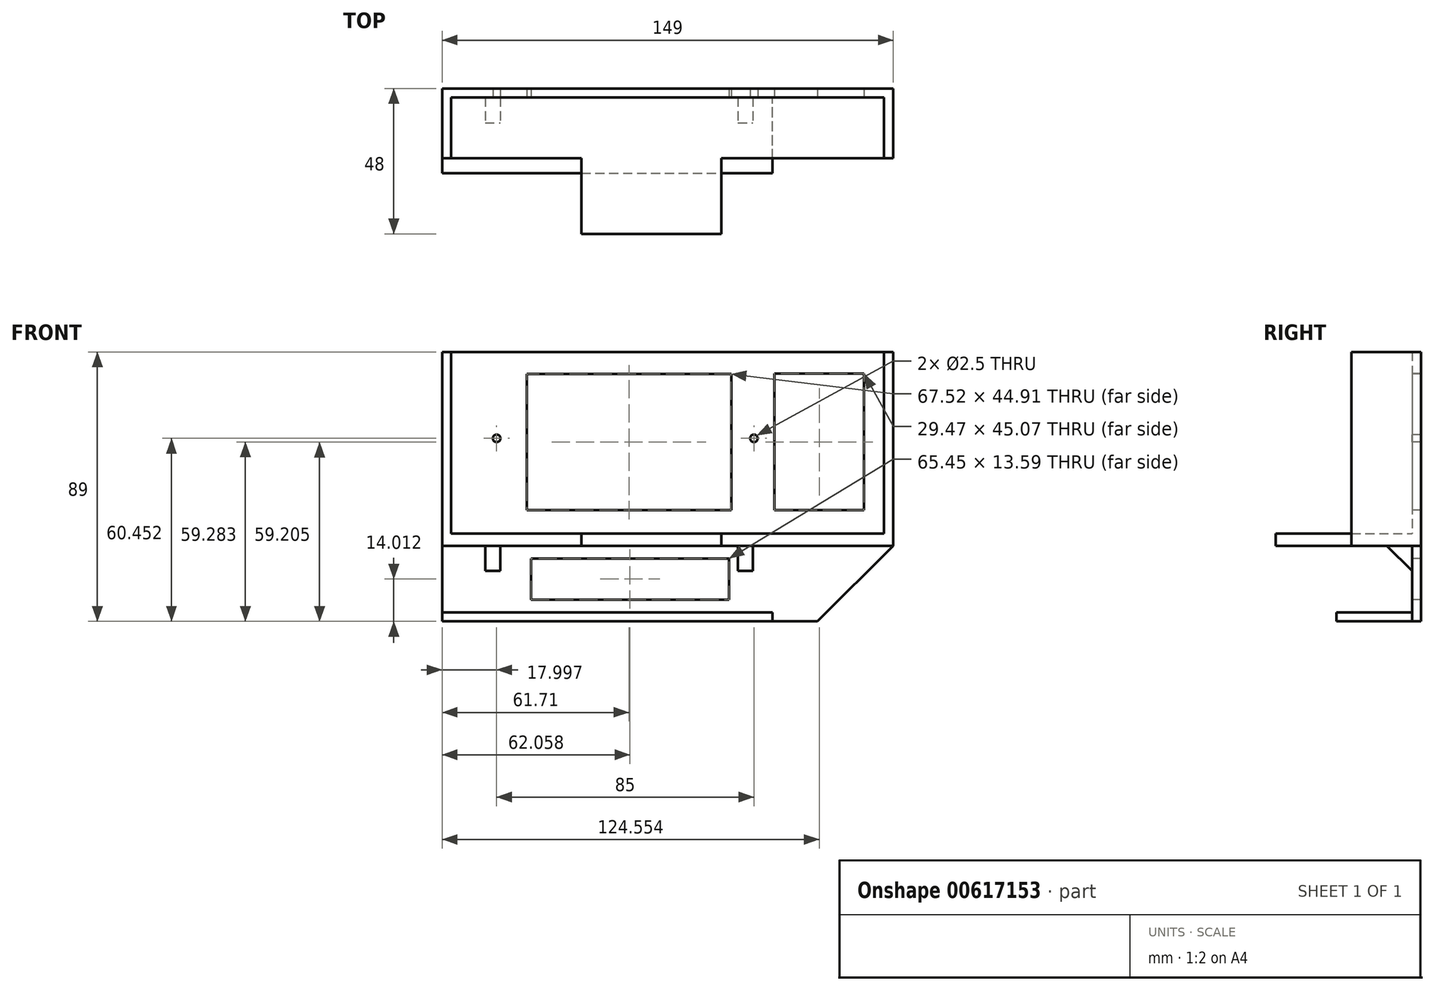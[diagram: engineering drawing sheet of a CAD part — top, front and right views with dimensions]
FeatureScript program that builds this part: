
annotation { "Feature Type Name" : "Feature", "Feature Type Description" : "" }
export const myFeature = defineFeature(function(context is Context, id is Id, definition is map)
    precondition{}
    {
        {
            var Q0;
            Q0=qCreatedBy(makeId("Front.planeOp"),FACE);
            var sketch = newSketch(context, id + "F0", { "sketchPlane" : qUnion([Q0])});
            skLineSegment(sketch, "E0.bottom", {"start": v(-34.14, 33.46) * mm, "end": v(112.86, 33.46) * mm});
            skLineSegment(sketch, "E0.top", {"start": v(-34.14, -26.54) * mm, "end": v(112.86, -26.54) * mm});
            skLineSegment(sketch, "E0.left", {"start": v(-34.14, 33.46) * mm, "end": v(-34.14, -26.54) * mm});
            skLineSegment(sketch, "E0.right", {"start": v(112.86, 33.46) * mm, "end": v(112.86, -26.54) * mm});
            skSolve(sketch);
        }
        {
            var Q0;
            Q0 = qSketchRegion(id + "F0", true);
            extrude(context, id + "F1", {"entities" : qUnion([Q0]), "depth" : 3 * mm, "offsetDistance" : 25 * mm});
        }
        {
            var Q0;
            Q0=makeQuery(id+"F1.opExtrude","CAP_FACE",FACE,{"disambiguationData":[OSD([sQuery(id+"F0.wireOp",EDGE,"E0.bottom"),sQuery(id+"F0.wireOp",EDGE,"E0.top"),sQuery(id+"F0.wireOp",EDGE,"E0.left"),sQuery(id+"F0.wireOp",EDGE,"E0.right")])],"isStart":false});
            var sketch = newSketch(context, id + "F2", { "sketchPlane" : qUnion([Q0])});
            skLineSegment(sketch, "E1.bottom", {"start": v(-34.14, 33.46) * mm, "end": v(-31.14, 33.46) * mm});
            skLineSegment(sketch, "E1.top", {"start": v(-34.14, -26.54) * mm, "end": v(-31.14, -26.54) * mm});
            skLineSegment(sketch, "E1.left", {"start": v(-34.14, 33.46) * mm, "end": v(-34.14, -26.54) * mm});
            skLineSegment(sketch, "E1.right", {"start": v(-31.14, 33.46) * mm, "end": v(-31.14, -26.54) * mm});
            skLineSegment(sketch, "E2.bottom", {"start": v(112.86, 33.46) * mm, "end": v(109.86, 33.46) * mm});
            skLineSegment(sketch, "E2.top", {"start": v(112.86, -26.54) * mm, "end": v(109.86, -26.54) * mm});
            skLineSegment(sketch, "E2.left", {"start": v(112.86, 33.46) * mm, "end": v(112.86, -26.54) * mm});
            skLineSegment(sketch, "E2.right", {"start": v(109.86, 33.46) * mm, "end": v(109.86, -26.54) * mm});
            skSolve(sketch);
        }
        {
            var Q0;
            Q0 = qSketchRegion(id + "F2", true);
            extrude(context, id + "F3", {"entities" : qUnion([Q0]), "operationType" : NewBodyOperationType.ADD, "depth" : 20 * mm, "offsetDistance" : 25 * mm});
        }
        {
            var Q0;
            Q0=makeQuery(id+"F3.boolean.opBoolean","MERGE",FACE,{"derivedFrom":[makeQuery(id+"F1.opExtrude","SWEPT_FACE",FACE,{"disambiguationData":[OSD([sQuery(id+"F0.wireOp",EDGE,"E0.top")])]}),makeQuery(id+"F3.opExtrude","SWEPT_FACE",FACE,{"disambiguationData":[OSD([sQuery(id+"F2.wireOp",EDGE,"E1.top")])]}),makeQuery(id+"F3.opExtrude","SWEPT_FACE",FACE,{"disambiguationData":[OSD([sQuery(id+"F2.wireOp",EDGE,"E2.top")])]})]});
            extrude(context, id + "F4", {"entities" : qUnion([Q0]), "operationType" : NewBodyOperationType.ADD, "depth" : 4 * mm, "offsetDistance" : 25 * mm});
        }
        {
            var Q0;
            {var subQ0=sQuery(id+"F0.wireOp",EDGE,"E0.top");Q0=makeQuery(id+"F4.boolean.opBoolean","MERGE",FACE,{"derivedFrom":[makeQuery(id+"F1.opExtrude","CAP_FACE",FACE,{"disambiguationData":[OSD([sQuery(id+"F0.wireOp",EDGE,"E0.bottom"),subQ0,sQuery(id+"F0.wireOp",EDGE,"E0.left"),sQuery(id+"F0.wireOp",EDGE,"E0.right")])],"isStart":false}),makeQuery(id+"F4.opExtrude","SWEPT_FACE",FACE,{"disambiguationData":[OSD([subQ0]),TDD([makeQuery(id+"F1.opExtrude","CAP_EDGE",EDGE,{"disambiguationData":[OSD([subQ0])],"isStart":false})])]})]});}
            var sketch = newSketch(context, id + "F5", { "sketchPlane" : qUnion([Q0])});
            skLineSegment(sketch, "E3.bottom", {"start": v(-31.14, -30.54) * mm, "end": v(109.86, -30.54) * mm});
            skLineSegment(sketch, "E3.top", {"start": v(-31.14, -26.54) * mm, "end": v(109.86, -26.54) * mm});
            skLineSegment(sketch, "E3.left", {"start": v(-31.14, -30.54) * mm, "end": v(-31.14, -26.54) * mm});
            skLineSegment(sketch, "E3.right", {"start": v(109.86, -30.54) * mm, "end": v(109.86, -26.54) * mm});
            skSolve(sketch);
        }
        {
            var Q0;
            Q0 = qSketchRegion(id + "F5", true);
            extrude(context, id + "F6", {"entities" : qUnion([Q0]), "operationType" : NewBodyOperationType.ADD, "depth" : 20 * mm, "offsetDistance" : 25 * mm});
        }
        {
            var Q0;
            {var subQ0=sQuery(id+"F2.wireOp",EDGE,"E2.left");var subQ1=sQuery(id+"F0.wireOp",EDGE,"E0.right");Q0=makeQuery(id+"F4.boolean.opBoolean","MERGE",FACE,{"derivedFrom":[makeQuery(id+"F3.boolean.opBoolean","MERGE",FACE,{"derivedFrom":[makeQuery(id+"F1.opExtrude","SWEPT_FACE",FACE,{"disambiguationData":[OSD([subQ1])]}),makeQuery(id+"F3.opExtrude","SWEPT_FACE",FACE,{"disambiguationData":[OSD([subQ0])]})]}),makeQuery(id+"F4.opExtrude","SWEPT_FACE",FACE,{"disambiguationData":[OSD([sQuery(id+"F0.wireOp",EDGE,"E0.top"),subQ1,sQuery(id+"F2.wireOp",EDGE,"E2.top"),subQ0])]})]});}
            extrude(context, id + "F7", {"entities" : qUnion([Q0]), "operationType" : NewBodyOperationType.ADD, "depth" : 2 * mm, "offsetDistance" : 25 * mm});
        }
        {
            var Q0;
            {var subQ0=sQuery(id+"F2.wireOp",EDGE,"E2.right");Q0=makeQuery(id+"F4.boolean.opBoolean","MERGE",FACE,{"derivedFrom":[makeQuery(id+"F3.opExtrude","SWEPT_FACE",FACE,{"disambiguationData":[OSD([subQ0])]}),makeQuery(id+"F4.opExtrude","SWEPT_FACE",FACE,{"disambiguationData":[OSD([sQuery(id+"F0.wireOp",EDGE,"E0.top"),sQuery(id+"F2.wireOp",EDGE,"E2.top"),subQ0])]})]});}
            extrude(context, id + "F8", {"entities" : qUnion([Q0]), "operationType" : NewBodyOperationType.REMOVE, "oppositeDirection" : true, "depth" : 2 * mm, "offsetDistance" : 25 * mm});
        }
        {
            var Q0;
            {var subQ0=sQuery(id+"F2.wireOp",EDGE,"E2.right");var subQ1=sQuery(id+"F2.wireOp",EDGE,"E2.top");var subQ2=sQuery(id+"F0.wireOp",EDGE,"E0.top");Q0=makeQuery(id+"F8.boolean.opBoolean","MERGE",FACE,{"derivedFrom":[makeQuery(id+"F4.boolean.opBoolean","MERGE",FACE,{"derivedFrom":[makeQuery(id+"F1.opExtrude","CAP_FACE",FACE,{"disambiguationData":[OSD([sQuery(id+"F0.wireOp",EDGE,"E0.bottom"),subQ2,sQuery(id+"F0.wireOp",EDGE,"E0.left"),sQuery(id+"F0.wireOp",EDGE,"E0.right")])],"isStart":false}),makeQuery(id+"F4.opExtrude","SWEPT_FACE",FACE,{"disambiguationData":[OSD([subQ2]),TDD([makeQuery(id+"F1.opExtrude","CAP_EDGE",EDGE,{"disambiguationData":[OSD([subQ2])],"isStart":false})])]})]}),makeQuery(id+"F8.opExtrude","SWEPT_FACE",FACE,{"disambiguationData":[OSD([subQ2,subQ1,subQ0]),TDD([makeQuery(id+"F4.boolean.opBoolean","MERGE",EDGE,{"derivedFrom":[makeQuery(id+"F3.opExtrude","CAP_EDGE",EDGE,{"disambiguationData":[OSD([subQ0])],"isStart":true}),makeQuery(id+"F4.opExtrude","SWEPT_EDGE",EDGE,{"disambiguationData":[OSD([subQ2,subQ1,subQ0]),TDD([makeQuery(id+"F3.opExtrude","CAP_VERTEX",VERTEX,{"disambiguationData":[OSD([subQ2,subQ1,subQ0])],"isStart":true})])]})]})])]})]});}
            var sketch = newSketch(context, id + "F9", { "sketchPlane" : qUnion([Q0])});
            skCircle(sketch, "E4", {"center": v(-16.14, 4.91) * mm, "radius": 1.25 * mm});
            skCircle(sketch, "E5", {"center": v(68.86, 4.91) * mm, "radius": 1.25 * mm});
            skSolve(sketch);
        }
        {
            var Q0;
            {var subQ0=sQuery(id+"F2.wireOp",EDGE,"E2.top");var subQ1=sQuery(id+"F0.wireOp",EDGE,"E0.top");Q0=makeQuery(id+"F7.boolean.opBoolean","MERGE",FACE,{"derivedFrom":[makeQuery(id+"F6.boolean.opBoolean","MERGE",FACE,{"derivedFrom":[makeQuery(id+"F4.opExtrude","CAP_FACE",FACE,{"disambiguationData":[OSD([subQ1,sQuery(id+"F2.wireOp",EDGE,"E1.top"),subQ0])],"isStart":false}),makeQuery(id+"F6.opExtrude","SWEPT_FACE",FACE,{"disambiguationData":[OSD([sQuery(id+"F5.wireOp",EDGE,"E3.bottom")])]})]}),makeQuery(id+"F7.opExtrude","SWEPT_FACE",FACE,{"disambiguationData":[OSD([subQ1,sQuery(id+"F0.wireOp",EDGE,"E0.right"),subQ0,sQuery(id+"F2.wireOp",EDGE,"E2.left")])]})]});}
            var sketch = newSketch(context, id + "F10", { "sketchPlane" : qUnion([Q0])});
            skLineSegment(sketch, "E6.bottom", {"start": v(-19.9, 0) * mm, "end": v(-14.9, 0) * mm});
            skLineSegment(sketch, "E6.top", {"start": v(-19.9, 11.3) * mm, "end": v(-14.9, 11.3) * mm});
            skLineSegment(sketch, "E6.left", {"start": v(-19.9, 0) * mm, "end": v(-19.9, 11.3) * mm});
            skLineSegment(sketch, "E6.right", {"start": v(-14.9, 0) * mm, "end": v(-14.9, 11.3) * mm});
            skLineSegment(sketch, "E7.bottom", {"start": v(63.56, 0) * mm, "end": v(68.56, 0) * mm});
            skLineSegment(sketch, "E7.top", {"start": v(63.56, 11.3) * mm, "end": v(68.56, 11.3) * mm});
            skLineSegment(sketch, "E7.left", {"start": v(63.56, 0) * mm, "end": v(63.56, 11.3) * mm});
            skLineSegment(sketch, "E7.right", {"start": v(68.56, 0) * mm, "end": v(68.56, 11.3) * mm});
            skSolve(sketch);
        }
        {
            var Q0;
            Q0=makeQuery(id+"F10.imprint","IMPRINT",FACE,{"disambiguationData":[TD([[makeQuery(id+"F10.imprint","IMPRINT",EDGE,{"derivedFrom":sQuery(id+"F10.wireOp",EDGE,"E6.bottom")}),1.0]])]});
            var Q1;
            Q1=makeQuery(id+"F10.imprint","IMPRINT",FACE,{"disambiguationData":[TD([[makeQuery(id+"F10.imprint","IMPRINT",EDGE,{"derivedFrom":sQuery(id+"F10.wireOp",EDGE,"E7.bottom")}),1.0]])]});
            extrude(context, id + "F11", {"entities" : qUnion([Q0, Q1]), "operationType" : NewBodyOperationType.ADD, "depth" : 15 * mm, "offsetDistance" : 25 * mm});
        }
        {
            var Q0;
            Q0=makeQuery(id+"F9.imprint","IMPRINT",FACE,{"disambiguationData":[TD([[makeQuery(id+"F9.imprint","IMPRINT",EDGE,{"derivedFrom":sQuery(id+"F9.wireOp",EDGE,"E4")}),1.0]])]});
            var Q1;
            Q1=makeQuery(id+"F9.imprint","IMPRINT",FACE,{"disambiguationData":[TD([[makeQuery(id+"F9.imprint","IMPRINT",EDGE,{"derivedFrom":sQuery(id+"F9.wireOp",EDGE,"E5")}),1.0]])]});
            extrude(context, id + "F12", {"entities" : qUnion([Q0, Q1]), "operationType" : NewBodyOperationType.REMOVE, "oppositeDirection" : true, "depth" : 25 * mm, "offsetDistance" : 25 * mm});
        }
        {
            var Q0;
            Q0=makeQuery(id+"F11.opExtrude","CAP_EDGE",EDGE,{"disambiguationData":[OSD([sQuery(id+"F10.wireOp",EDGE,"E6.top")])],"isStart":false});
            var Q1;
            Q1=makeQuery(id+"F11.opExtrude","CAP_EDGE",EDGE,{"disambiguationData":[OSD([sQuery(id+"F10.wireOp",EDGE,"E7.top")])],"isStart":false});
            chamfer(context, id + "F13", {"entities" : qUnion([Q0, Q1]), "width" : 15 * mm, "tangentPropagation" : true});
        }
        {
            var Q0;
            {var subQ0=sQuery(id+"F2.wireOp",EDGE,"E2.top");var subQ1=sQuery(id+"F0.wireOp",EDGE,"E0.top");Q0=makeQuery(id+"F7.boolean.opBoolean","MERGE",FACE,{"derivedFrom":[makeQuery(id+"F6.boolean.opBoolean","MERGE",FACE,{"derivedFrom":[makeQuery(id+"F4.opExtrude","CAP_FACE",FACE,{"disambiguationData":[OSD([subQ1,sQuery(id+"F2.wireOp",EDGE,"E1.top"),subQ0])],"isStart":false}),makeQuery(id+"F6.opExtrude","SWEPT_FACE",FACE,{"disambiguationData":[OSD([sQuery(id+"F5.wireOp",EDGE,"E3.bottom")])]})]}),makeQuery(id+"F7.opExtrude","SWEPT_FACE",FACE,{"disambiguationData":[OSD([subQ1,sQuery(id+"F0.wireOp",EDGE,"E0.right"),subQ0,sQuery(id+"F2.wireOp",EDGE,"E2.left")])]})]});}
            var sketch = newSketch(context, id + "F14", { "sketchPlane" : qUnion([Q0])});
            skLineSegment(sketch, "E8.bottom", {"start": v(-34.14, 0) * mm, "end": v(114.86, 0) * mm});
            skLineSegment(sketch, "E8.top", {"start": v(-34.14, 3) * mm, "end": v(114.86, 3) * mm});
            skLineSegment(sketch, "E8.left", {"start": v(-34.14, 0) * mm, "end": v(-34.14, 3) * mm});
            skLineSegment(sketch, "E8.right", {"start": v(114.86, 0) * mm, "end": v(114.86, 3) * mm});
            skSolve(sketch);
        }
        {
            var Q0;
            {var subQ0=sQuery(id+"F14.wireOp",EDGE,"E8.left");Q0=makeQuery(id+"F14.imprint","IMPRINT",FACE,{"disambiguationData":[TD([[makeQuery(id+"F14.imprint","IMPRINT",EDGE,{"derivedFrom":subQ0}),1.0]])]});}
            var Q1;
            {var subQ0=sQuery(id+"F14.wireOp",EDGE,"E8.right");Q1=makeQuery(id+"F14.imprint","IMPRINT",FACE,{"disambiguationData":[TD([[makeQuery(id+"F14.imprint","IMPRINT",EDGE,{"derivedFrom":subQ0}),-1.0]])]});}
            var Q2;
            {var subQ0=sQuery(id+"F14.wireOp",EDGE,"E8.bottom");var subQ1=makeQuery(id+"F11.opExtrude","CAP_EDGE",EDGE,{"disambiguationData":[OSD([sQuery(id+"F10.wireOp",EDGE,"E6.left")])],"isStart":true});var subQ2=makeQuery(id+"F14.imprint","INTERSECT",VERTEX,{"derivedFrom":[subQ1,subQ0]});Q2=makeQuery(id+"F14.imprint","IMPRINT",FACE,{"disambiguationData":[TD([[makeQuery(id+"F14.imprint","IMPRINT",EDGE,{"disambiguationData":[TD([[subQ2,-1.0]])],"derivedFrom":subQ0}),1.0]])]});}
            var Q3;
            {var subQ0=sQuery(id+"F14.wireOp",EDGE,"E8.bottom");var subQ1=makeQuery(id+"F11.opExtrude","CAP_EDGE",EDGE,{"disambiguationData":[OSD([sQuery(id+"F10.wireOp",EDGE,"E7.left")])],"isStart":true});var subQ2=makeQuery(id+"F14.imprint","INTERSECT",VERTEX,{"derivedFrom":[subQ1,subQ0]});Q3=makeQuery(id+"F14.imprint","IMPRINT",FACE,{"disambiguationData":[TD([[makeQuery(id+"F14.imprint","IMPRINT",EDGE,{"disambiguationData":[TD([[subQ2,-1.0]])],"derivedFrom":subQ0}),1.0]])]});}
            var Q4;
            {var subQ0=sQuery(id+"F14.wireOp",EDGE,"E8.bottom");var subQ1=makeQuery(id+"F11.opExtrude","CAP_EDGE",EDGE,{"disambiguationData":[OSD([sQuery(id+"F10.wireOp",EDGE,"E6.right")])],"isStart":true});var subQ2=makeQuery(id+"F14.imprint","INTERSECT",VERTEX,{"derivedFrom":[subQ1,subQ0]});Q4=makeQuery(id+"F14.imprint","IMPRINT",FACE,{"disambiguationData":[TD([[makeQuery(id+"F14.imprint","IMPRINT",EDGE,{"disambiguationData":[TD([[subQ2,-1.0]])],"derivedFrom":subQ0}),1.0]])]});}
            extrude(context, id + "F15", {"entities" : qUnion([Q0, Q1, Q2, Q3, Q4]), "operationType" : NewBodyOperationType.ADD, "depth" : 25 * mm, "offsetDistance" : 25 * mm});
        }
        {
            var Q0;
            Q0=makeQuery(id+"F15.opExtrude","CAP_EDGE",EDGE,{"disambiguationData":[OSD([sQuery(id+"F14.wireOp",EDGE,"E8.right")])],"isStart":false});
            chamfer(context, id + "F16", {"entities" : qUnion([Q0]), "width" : 25 * mm, "tangentPropagation" : true});
        }
        {
            var Q0;
            Q0=makeQuery(id+"F15.opExtrude","SWEPT_FACE",FACE,{"disambiguationData":[OSD([sQuery(id+"F14.wireOp",EDGE,"E8.top")])]});
            var sketch = newSketch(context, id + "F17", { "sketchPlane" : qUnion([Q0])});
            skLineSegment(sketch, "E9.bottom", {"start": v(-34.14, -55.54) * mm, "end": v(74.97, -55.54) * mm});
            skLineSegment(sketch, "E9.top", {"start": v(-34.14, -52.54) * mm, "end": v(74.97, -52.54) * mm});
            skLineSegment(sketch, "E9.left", {"start": v(-34.14, -55.54) * mm, "end": v(-34.14, -52.54) * mm});
            skLineSegment(sketch, "E9.right", {"start": v(74.97, -55.54) * mm, "end": v(74.97, -52.54) * mm});
            skSolve(sketch);
        }
        {
            var Q0;
            Q0 = qSketchRegion(id + "F17", true);
            extrude(context, id + "F18", {"entities" : qUnion([Q0]), "operationType" : NewBodyOperationType.ADD, "depth" : 25 * mm, "offsetDistance" : 25 * mm});
        }
        {
            var Q0;
            {var subQ0=sQuery(id+"F2.wireOp",EDGE,"E2.right");var subQ1=sQuery(id+"F2.wireOp",EDGE,"E2.top");var subQ2=sQuery(id+"F0.wireOp",EDGE,"E0.top");Q0=makeQuery(id+"F8.boolean.opBoolean","MERGE",FACE,{"derivedFrom":[makeQuery(id+"F4.boolean.opBoolean","MERGE",FACE,{"derivedFrom":[makeQuery(id+"F1.opExtrude","CAP_FACE",FACE,{"disambiguationData":[OSD([sQuery(id+"F0.wireOp",EDGE,"E0.bottom"),subQ2,sQuery(id+"F0.wireOp",EDGE,"E0.left"),sQuery(id+"F0.wireOp",EDGE,"E0.right")])],"isStart":false}),makeQuery(id+"F4.opExtrude","SWEPT_FACE",FACE,{"disambiguationData":[OSD([subQ2]),TDD([makeQuery(id+"F1.opExtrude","CAP_EDGE",EDGE,{"disambiguationData":[OSD([subQ2])],"isStart":false})])]})]}),makeQuery(id+"F8.opExtrude","SWEPT_FACE",FACE,{"disambiguationData":[OSD([subQ2,subQ1,subQ0]),TDD([makeQuery(id+"F4.boolean.opBoolean","MERGE",EDGE,{"derivedFrom":[makeQuery(id+"F3.opExtrude","CAP_EDGE",EDGE,{"disambiguationData":[OSD([subQ0])],"isStart":true}),makeQuery(id+"F4.opExtrude","SWEPT_EDGE",EDGE,{"disambiguationData":[OSD([subQ2,subQ1,subQ0]),TDD([makeQuery(id+"F3.opExtrude","CAP_VERTEX",VERTEX,{"disambiguationData":[OSD([subQ2,subQ1,subQ0])],"isStart":true})])]})]})])]})]});}
            var sketch = newSketch(context, id + "F19", { "sketchPlane" : qUnion([Q0])});
            skLineSegment(sketch, "E10.bottom", {"start": v(-6.2, 26.12) * mm, "end": v(61.33, 26.12) * mm});
            skLineSegment(sketch, "E10.top", {"start": v(-6.2, -18.8) * mm, "end": v(61.33, -18.8) * mm});
            skLineSegment(sketch, "E10.left", {"start": v(-6.2, 26.12) * mm, "end": v(-6.2, -18.8) * mm});
            skLineSegment(sketch, "E10.right", {"start": v(61.33, 26.12) * mm, "end": v(61.33, -18.8) * mm});
            skLineSegment(sketch, "E11.bottom", {"start": v(75.68, 26.28) * mm, "end": v(105.15, 26.28) * mm});
            skLineSegment(sketch, "E11.top", {"start": v(75.68, -18.8) * mm, "end": v(105.15, -18.8) * mm});
            skLineSegment(sketch, "E11.left", {"start": v(75.68, 26.28) * mm, "end": v(75.68, -18.8) * mm});
            skLineSegment(sketch, "E11.right", {"start": v(105.15, 26.28) * mm, "end": v(105.15, -18.8) * mm});
            skSolve(sketch);
        }
        {
            var Q0;
            Q0 = qSketchRegion(id + "F19", true);
            extrude(context, id + "F20", {"entities" : qUnion([Q0]), "operationType" : NewBodyOperationType.REMOVE, "oppositeDirection" : true, "depth" : 25 * mm, "offsetDistance" : 25 * mm});
        }
        {
            var Q0;
            Q0=makeQuery(id+"F15.opExtrude","SWEPT_FACE",FACE,{"disambiguationData":[OSD([sQuery(id+"F14.wireOp",EDGE,"E8.top")])]});
            var sketch = newSketch(context, id + "F21", { "sketchPlane" : qUnion([Q0])});
            skLineSegment(sketch, "E12.bottom", {"start": v(-4.8, -34.73) * mm, "end": v(60.64, -34.73) * mm});
            skLineSegment(sketch, "E12.top", {"start": v(-4.8, -48.32) * mm, "end": v(60.64, -48.32) * mm});
            skLineSegment(sketch, "E12.left", {"start": v(-4.8, -34.73) * mm, "end": v(-4.8, -48.32) * mm});
            skLineSegment(sketch, "E12.right", {"start": v(60.64, -34.73) * mm, "end": v(60.64, -48.32) * mm});
            skSolve(sketch);
        }
        {
            var Q0;
            Q0 = qSketchRegion(id + "F21", true);
            extrude(context, id + "F22", {"entities" : qUnion([Q0]), "operationType" : NewBodyOperationType.REMOVE, "oppositeDirection" : true, "depth" : 25 * mm, "offsetDistance" : 25 * mm});
        }
        {
            var Q0;
            {var subQ0=sQuery(id+"F2.wireOp",EDGE,"E2.left");var subQ1=sQuery(id+"F2.wireOp",EDGE,"E2.top");var subQ2=sQuery(id+"F2.wireOp",EDGE,"E1.top");Q0=makeQuery(id+"F7.boolean.opBoolean","MERGE",FACE,{"derivedFrom":[makeQuery(id+"F6.boolean.opBoolean","MERGE",FACE,{"derivedFrom":[makeQuery(id+"F4.boolean.opBoolean","MERGE",FACE,{"derivedFrom":[makeQuery(id+"F3.opExtrude","CAP_FACE",FACE,{"disambiguationData":[OSD([sQuery(id+"F2.wireOp",EDGE,"E1.bottom"),subQ2,sQuery(id+"F2.wireOp",EDGE,"E1.left"),sQuery(id+"F2.wireOp",EDGE,"E1.right")])],"isStart":false}),makeQuery(id+"F4.opExtrude","SWEPT_FACE",FACE,{"disambiguationData":[OSD([subQ2])]})]}),makeQuery(id+"F4.boolean.opBoolean","MERGE",FACE,{"derivedFrom":[makeQuery(id+"F3.opExtrude","CAP_FACE",FACE,{"disambiguationData":[OSD([sQuery(id+"F2.wireOp",EDGE,"E2.bottom"),subQ1,subQ0,sQuery(id+"F2.wireOp",EDGE,"E2.right")])],"isStart":false}),makeQuery(id+"F4.opExtrude","SWEPT_FACE",FACE,{"disambiguationData":[OSD([subQ1])]})]}),makeQuery(id+"F6.opExtrude","CAP_FACE",FACE,{"disambiguationData":[OSD([sQuery(id+"F5.wireOp",EDGE,"E3.bottom"),sQuery(id+"F5.wireOp",EDGE,"E3.top"),sQuery(id+"F5.wireOp",EDGE,"E3.left"),sQuery(id+"F5.wireOp",EDGE,"E3.right")])],"isStart":false})]}),makeQuery(id+"F7.opExtrude","SWEPT_FACE",FACE,{"disambiguationData":[OSD([subQ1,subQ0])]})]});}
            var sketch = newSketch(context, id + "F23", { "sketchPlane" : qUnion([Q0])});
            skLineSegment(sketch, "E13.bottom", {"start": v(11.9, -26.54) * mm, "end": v(58.06, -26.54) * mm});
            skLineSegment(sketch, "E13.top", {"start": v(11.9, -30.54) * mm, "end": v(58.06, -30.54) * mm});
            skLineSegment(sketch, "E13.left", {"start": v(11.9, -26.54) * mm, "end": v(11.9, -30.54) * mm});
            skLineSegment(sketch, "E13.right", {"start": v(58.06, -26.54) * mm, "end": v(58.06, -30.54) * mm});
            skSolve(sketch);
        }
        {
            var Q0;
            Q0 = qSketchRegion(id + "F23", true);
            extrude(context, id + "F24", {"entities" : qUnion([Q0]), "operationType" : NewBodyOperationType.ADD, "depth" : 25 * mm, "offsetDistance" : 25 * mm});
        }
    });
